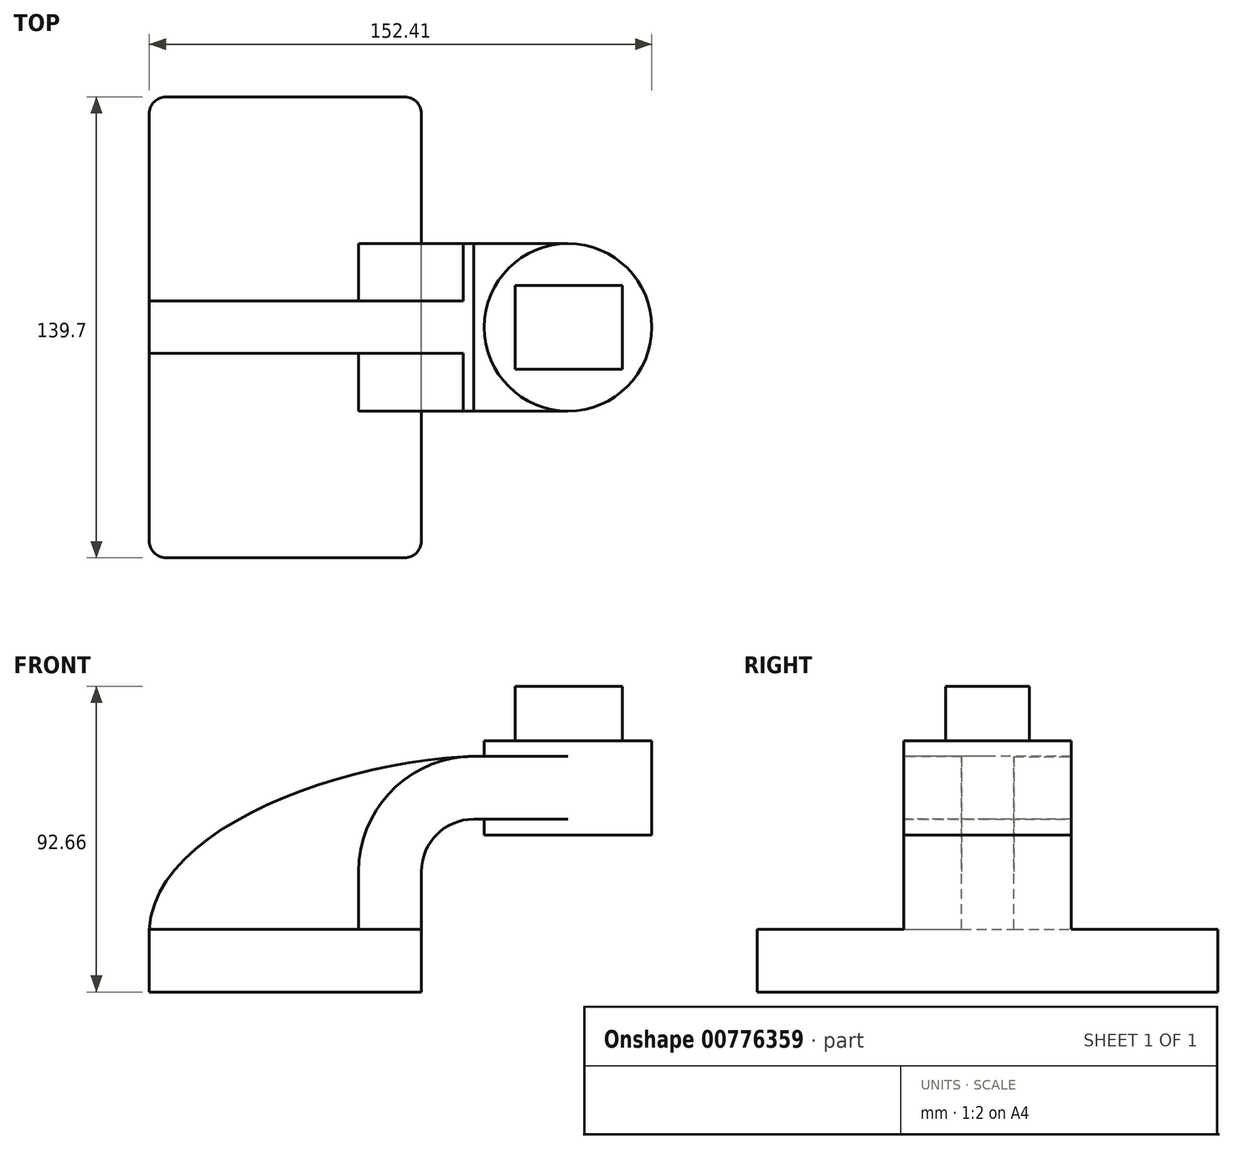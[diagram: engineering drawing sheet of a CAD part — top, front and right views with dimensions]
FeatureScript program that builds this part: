
annotation { "Feature Type Name" : "Feature", "Feature Type Description" : "" }
export const myFeature = defineFeature(function(context is Context, id is Id, definition is map)
    precondition{}
    {
        {
            var Q0;
            Q0=qCreatedBy(makeId("Front.planeOp"),FACE);
            var sketch = newSketch(context, id + "F0", { "sketchPlane" : qUnion([Q0])});
            skLineSegment(sketch, "E0.rect.bottom", {"start": v(-41.28, 9.52) * mm, "end": v(41.28, 9.52) * mm});
            skLineSegment(sketch, "E0.rect.top", {"start": v(-41.28, -9.52) * mm, "end": v(41.28, -9.52) * mm});
            skLineSegment(sketch, "E0.rect.left", {"start": v(-41.28, 9.52) * mm, "end": v(-41.28, -9.52) * mm});
            skLineSegment(sketch, "E0.rect.right", {"start": v(41.28, 9.52) * mm, "end": v(41.28, -9.52) * mm});
            skPoint(sketch, "E0.rect.middle", {"position": v(0, 0) * mm});
            skLineSegment(sketch, "E1", {"start": v(41.28, 9.52) * mm, "end": v(41.28, 27) * mm});
            skArc(sketch, "E2", {"start": v(41.28, 27) * mm, "mid": v(45.92, 38.23) * mm, "end": v(57.15, 42.88) * mm});
            skLineSegment(sketch, "E3", {"start": v(57.15, 42.88) * mm, "end": v(85.72, 42.88) * mm});
            skLineSegment(sketch, "E4.rect.bottom", {"start": v(60.32, 38.1) * mm, "end": v(111.12, 38.1) * mm});
            skLineSegment(sketch, "E4.rect.top", {"start": v(60.32, 66.68) * mm, "end": v(111.12, 66.68) * mm});
            skLineSegment(sketch, "E4.rect.left", {"start": v(60.32, 38.1) * mm, "end": v(60.32, 66.68) * mm});
            skLineSegment(sketch, "E4.rect.right", {"start": v(111.13, 38.1) * mm, "end": v(111.12, 66.68) * mm});
            skPoint(sketch, "E4.rect.middle", {"position": v(85.72, 52.39) * mm});
            skLineSegment(sketch, "E5.0", {"start": v(57.15, 61.93) * mm, "end": v(85.72, 61.93) * mm});
            skArc(sketch, "E5.1", {"start": v(22.23, 27) * mm, "mid": v(32.45, 51.7) * mm, "end": v(57.15, 61.93) * mm});
            skLineSegment(sketch, "E5.2", {"start": v(22.23, 9.52) * mm, "end": v(22.23, 27) * mm});
            skLineSegment(sketch, "E6", {"start": v(85.72, 38.1) * mm, "end": v(85.72, 66.68) * mm});
            skFitSpline(sketch, "E7", {"points": [v(-41.28, 9.53) * mm, v(57.15, 61.93) * mm], "startDerivative": vector(5.2, 92.34) * mm, "endDerivative": vector(120.92, 4.22) * mm});
            skLineSegment(sketch, "E8.bottom", {"start": v(69.66, 83.13) * mm, "end": v(102.18, 83.13) * mm});
            skLineSegment(sketch, "E8.top", {"start": v(69.66, 66.68) * mm, "end": v(102.18, 66.68) * mm});
            skLineSegment(sketch, "E8.left", {"start": v(69.66, 83.13) * mm, "end": v(69.66, 66.68) * mm});
            skLineSegment(sketch, "E8.right", {"start": v(102.18, 83.13) * mm, "end": v(102.18, 66.68) * mm});
            skSolve(sketch);
        }
        {
            var Q0;
            Q0=makeQuery(id+"F0.imprint","IMPRINT",FACE,{"disambiguationData":[TD([[makeQuery(id+"F0.imprint","IMPRINT",EDGE,{"derivedFrom":sQuery(id+"F0.wireOp",EDGE,"E0.rect.top")}),1.0]])]});
            extrude(context, id + "F1", {"entities" : qUnion([Q0]), "endBound" : BoundingType.SYMMETRIC, "depth" : 139.7 * mm, "offsetDistance" : 25.4 * mm});
        }
        {
            var Q0;
            {var subQ9=sQuery(id+"F0.wireOp",EDGE,"E1");Q0=makeQuery(id+"F0.imprint","IMPRINT",FACE,{"disambiguationData":[TD([[makeQuery(id+"F0.imprint","IMPRINT",EDGE,{"derivedFrom":subQ9}),1.0]])]});}
            var Q1;
            {var subQ0=sQuery(id+"F0.wireOp",EDGE,"E6");var subQ1=sQuery(id+"F0.wireOp",EDGE,"E3");var subQ2=makeQuery(id+"F0.imprint","INTERSECT",VERTEX,{"derivedFrom":[subQ1,subQ0]});Q1=makeQuery(id+"F0.imprint","IMPRINT",FACE,{"disambiguationData":[TD([[makeQuery(id+"F0.imprint","IMPRINT",EDGE,{"disambiguationData":[TD([[subQ2,1.0]])],"derivedFrom":subQ1}),1.0]])]});}
            extrude(context, id + "F2", {"entities" : qUnion([Q0, Q1]), "operationType" : NewBodyOperationType.ADD, "endBound" : BoundingType.SYMMETRIC, "depth" : 50.8 * mm});
        }
        {
            var Q0;
            {var subQ3=sQuery(id+"F0.wireOp",EDGE,"E5.2");Q0=makeQuery(id+"F0.imprint","IMPRINT",FACE,{"disambiguationData":[TD([[makeQuery(id+"F0.imprint","IMPRINT",EDGE,{"derivedFrom":subQ3}),1.0]])]});}
            extrude(context, id + "F3", {"entities" : qUnion([Q0]), "operationType" : NewBodyOperationType.ADD, "endBound" : BoundingType.SYMMETRIC, "depth" : 15.88 * mm});
        }
        {
            var Q0;
            {var subQ5=sQuery(id+"F0.wireOp",EDGE,"E4.rect.right");Q0=makeQuery(id+"F0.imprint","IMPRINT",FACE,{"disambiguationData":[TD([[makeQuery(id+"F0.imprint","IMPRINT",EDGE,{"derivedFrom":subQ5}),1.0]])]});}
            var Q1;
            Q1=sQuery(id+"F0.wireOp",EDGE,"E6");
            revolve(context, id + "F4", {"operationType" : NewBodyOperationType.ADD, "entities" : qUnion([Q0]), "axis" : qUnion([Q1]), "revolveType" : RevolveType.FULL});
        }
        {
            var Q0;
            Q0=makeQuery(id+"F1.opExtrude","CAP_EDGE",EDGE,{"disambiguationData":[OSD([sQuery(id+"F0.wireOp",EDGE,"E0.rect.right")])],"isStart":false});
            var Q1;
            Q1=makeQuery(id+"F1.opExtrude","CAP_EDGE",EDGE,{"disambiguationData":[OSD([sQuery(id+"F0.wireOp",EDGE,"E0.rect.left")])],"isStart":false});
            var Q2;
            Q2=makeQuery(id+"F1.opExtrude","CAP_EDGE",EDGE,{"disambiguationData":[OSD([sQuery(id+"F0.wireOp",EDGE,"E0.rect.right")])],"isStart":true});
            var Q3;
            Q3=makeQuery(id+"F1.opExtrude","CAP_EDGE",EDGE,{"disambiguationData":[OSD([sQuery(id+"F0.wireOp",EDGE,"E0.rect.left")])],"isStart":true});
            fillet(context, id + "F5", {"entities" : qUnion([Q0, Q1, Q2, Q3]), "radius" : 5.08 * mm, "tangentPropagation" : true, "allowEdgeOverflow" : false});
        }
        {
            var Q0;
            Q0=makeQuery(id+"F0.imprint","IMPRINT",FACE,{"disambiguationData":[TD([[makeQuery(id+"F0.imprint","IMPRINT",EDGE,{"derivedFrom":sQuery(id+"F0.wireOp",EDGE,"E8.bottom")}),-1.0]])]});
            extrude(context, id + "F6", {"entities" : qUnion([Q0]), "operationType" : NewBodyOperationType.ADD, "endBound" : BoundingType.SYMMETRIC, "depth" : 25.4 * mm, "offsetDistance" : 25.4 * mm});
        }
    });
